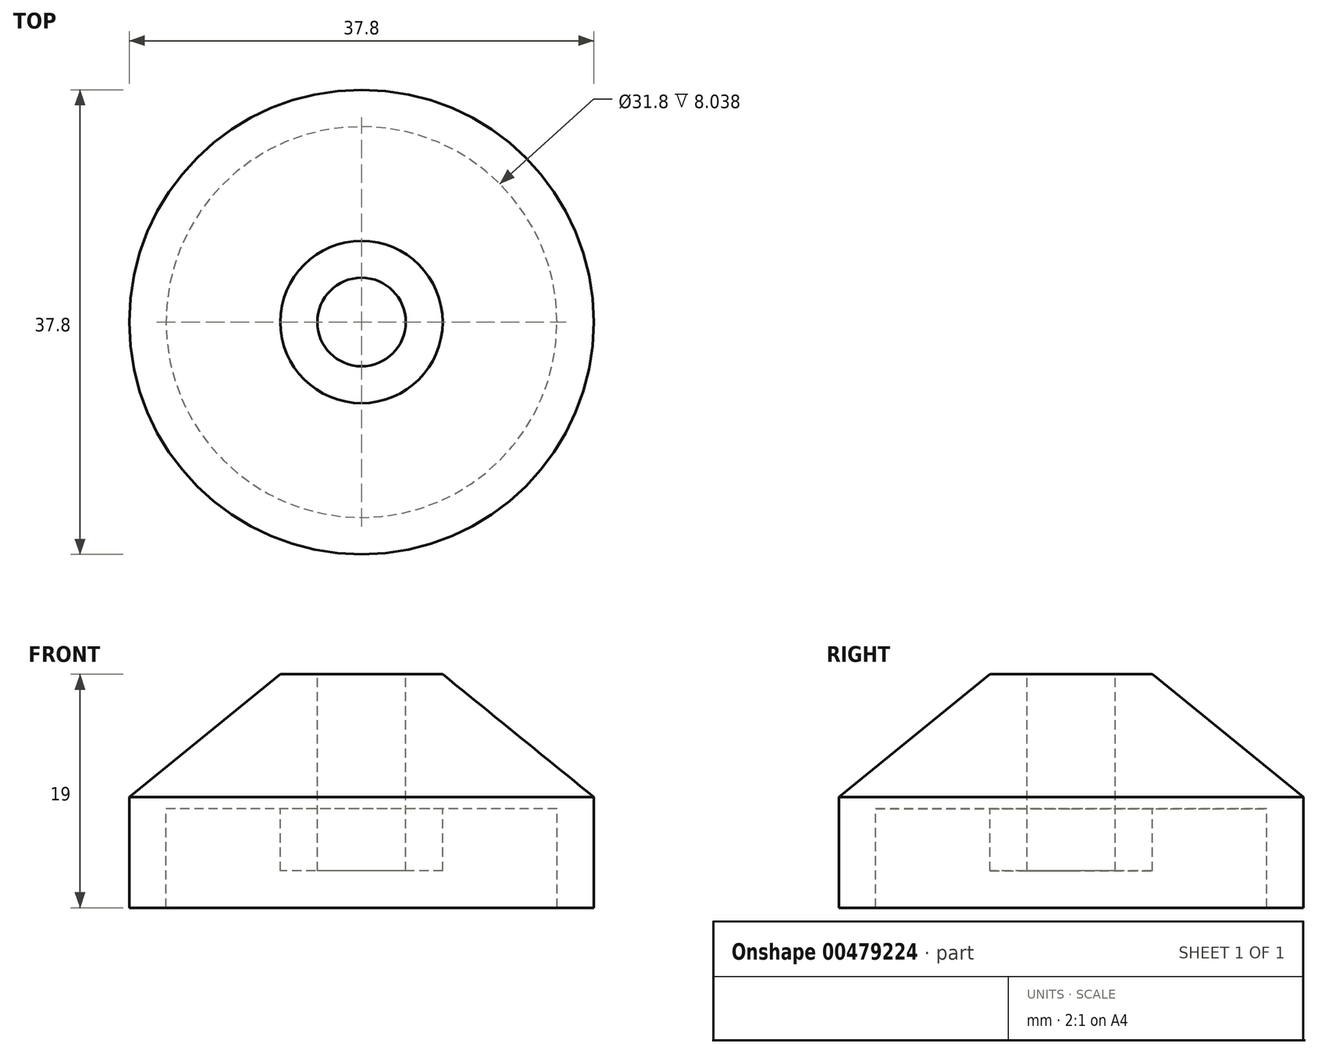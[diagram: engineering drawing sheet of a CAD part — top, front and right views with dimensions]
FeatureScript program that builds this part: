
annotation { "Feature Type Name" : "Feature", "Feature Type Description" : "" }
export const myFeature = defineFeature(function(context is Context, id is Id, definition is map)
    precondition{}
    {
        {
            var Q0;
            Q0=qCreatedBy(makeId("Front.planeOp"),FACE);
            var sketch = newSketch(context, id + "F0", { "sketchPlane" : qUnion([Q0])});
            skLineSegment(sketch, "E0", {"start": v(-18.9, 0) * mm, "end": v(-18.9, 9) * mm});
            skLineSegment(sketch, "E1", {"start": v(0, 2.9) * mm, "end": v(0, 0) * mm});
            skLineSegment(sketch, "E2", {"start": v(-15.9, 0) * mm, "end": v(-15.9, 0.48) * mm});
            skLineSegment(sketch, "E3", {"start": v(-6.6, 3) * mm, "end": v(-3.6, 3) * mm});
            skLineSegment(sketch, "E4", {"start": v(-15.9, 0) * mm, "end": v(-18.9, 0) * mm});
            skLineSegment(sketch, "E5", {"start": v(-3.6, 9) * mm, "end": v(0, 9) * mm});
            skLineSegment(sketch, "E6", {"start": v(-3.6, 9) * mm, "end": v(-3.6, 19) * mm});
            skLineSegment(sketch, "E7", {"start": v(-3.6, 9) * mm, "end": v(-3.6, 3) * mm});
            skLineSegment(sketch, "E8", {"start": v(-15.9, 0.48) * mm, "end": v(-15.9, 3) * mm});
            skLineSegment(sketch, "E9", {"start": v(-15.9, 3) * mm, "end": v(-15.9, 8.04) * mm});
            skLineSegment(sketch, "E10", {"start": v(-15.9, 8.04) * mm, "end": v(-6.6, 8.04) * mm});
            skLineSegment(sketch, "E11", {"start": v(-6.6, 8.04) * mm, "end": v(-6.6, 3) * mm});
            skLineSegment(sketch, "E12", {"start": v(-3.6, 19) * mm, "end": v(-6.6, 19) * mm});
            skLineSegment(sketch, "E13", {"start": v(-6.6, 19) * mm, "end": v(-18.9, 9) * mm});
            skLineSegment(sketch, "E14", {"start": v(0, 9) * mm, "end": v(0, 19.17) * mm});
            skSolve(sketch);
        }
        {
            var Q0;
            {var subQ0=sQuery(id+"F0.wireOp",EDGE,"E0");Q0=makeQuery(id+"F0.imprint","IMPRINT",FACE,{"disambiguationData":[TD([[makeQuery(id+"F0.imprint","IMPRINT",EDGE,{"derivedFrom":subQ0}),-1.0]])]});}
            var Q1;
            Q1=sQuery(id+"F0.wireOp",EDGE,"E1");
            revolve(context, id + "F1", {"entities" : qUnion([Q0]), "axis" : qUnion([Q1]), "revolveType" : RevolveType.FULL});
        }
    });
